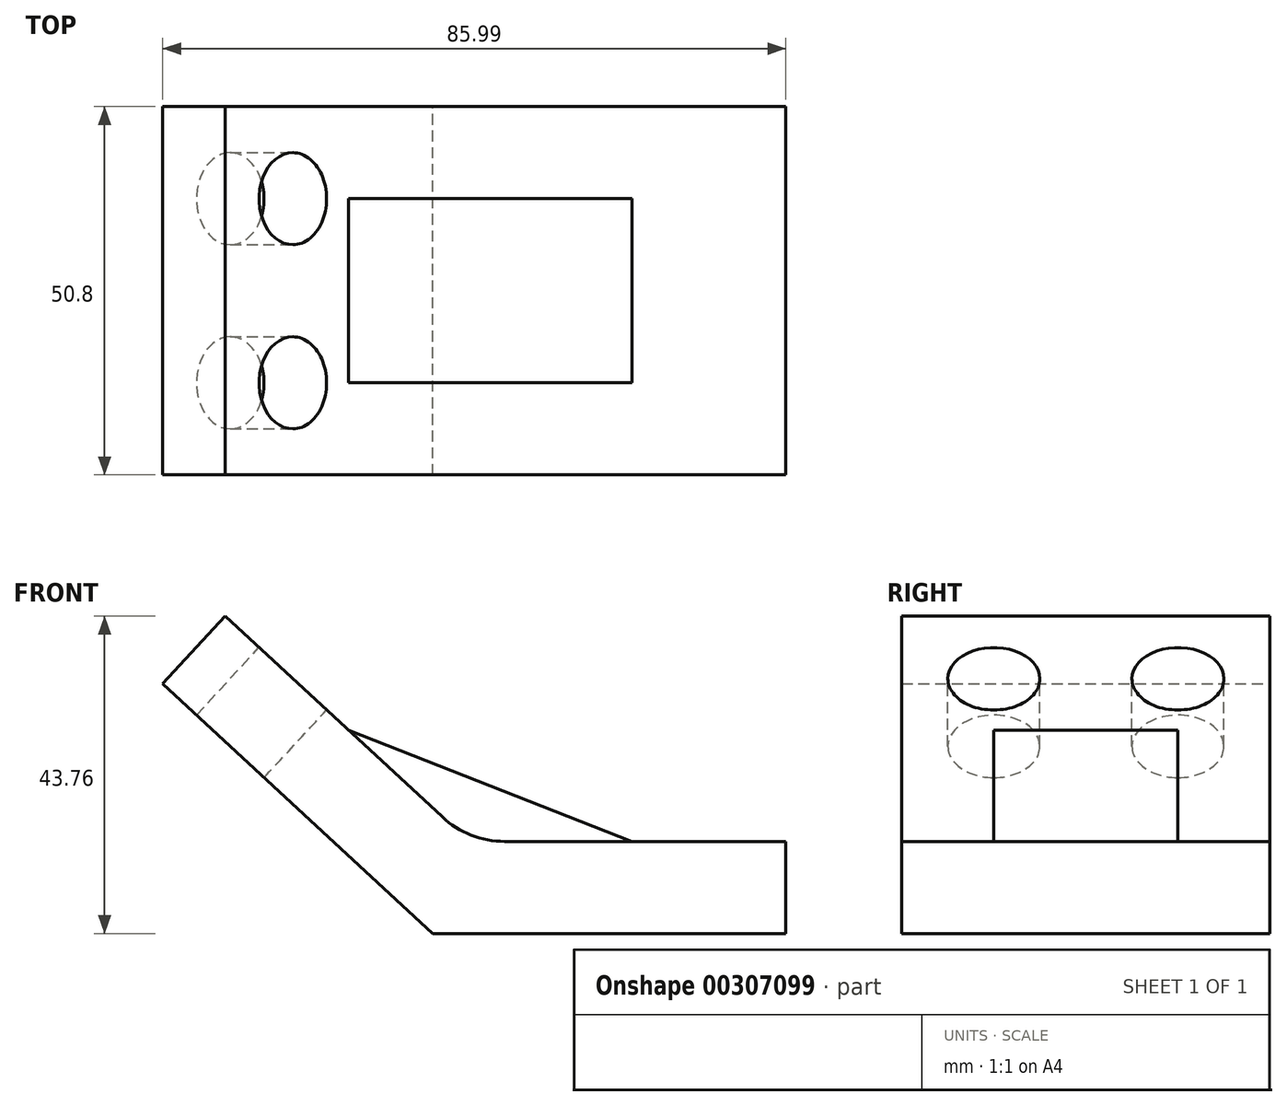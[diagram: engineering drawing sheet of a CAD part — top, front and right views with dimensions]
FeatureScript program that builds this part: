
annotation { "Feature Type Name" : "Feature", "Feature Type Description" : "" }
export const myFeature = defineFeature(function(context is Context, id is Id, definition is map)
    precondition{}
    {
        {
            var Q0;
            Q0=qCreatedBy(makeId("Front.planeOp"),FACE);
            var sketch = newSketch(context, id + "F0", { "sketchPlane" : qUnion([Q0])});
            skLineSegment(sketch, "E0", {"start": v(0, 0) * mm, "end": v(48.74, 0) * mm});
            skLineSegment(sketch, "E1", {"start": v(48.74, 0) * mm, "end": v(48.74, 12.7) * mm});
            skLineSegment(sketch, "E2", {"start": v(48.74, 12.7) * mm, "end": v(4.97, 12.7) * mm});
            skLineSegment(sketch, "E3", {"start": v(4.97, 12.7) * mm, "end": v(-28.63, 43.76) * mm});
            skLineSegment(sketch, "E4", {"start": v(-28.63, 43.76) * mm, "end": v(-37.25, 34.43) * mm});
            skLineSegment(sketch, "E5", {"start": v(-37.25, 34.43) * mm, "end": v(0, 0) * mm});
            skSolve(sketch);
        }
        {
            var Q0;
            Q0 = qSketchRegion(id + "F0", true);
            extrude(context, id + "F1", {"entities" : qUnion([Q0]), "endBound" : BoundingType.SYMMETRIC, "depth" : 50.8 * mm});
        }
        {
            var Q0;
            Q0=makeQuery(id+"F1.opExtrude","SWEPT_EDGE",EDGE,{"disambiguationData":[OSD([sQuery(id+"F0.wireOp",EDGE,"E2"),sQuery(id+"F0.wireOp",EDGE,"E3")])]});
            fillet(context, id + "F2", {"entities" : qUnion([Q0]), "radius" : 12.7 * mm, "tangentPropagation" : true, "allowEdgeOverflow" : false});
        }
        {
            var Q0;
            Q0=qCreatedBy(makeId("Front.planeOp"),FACE);
            var sketch = newSketch(context, id + "F3", { "sketchPlane" : qUnion([Q0])});
            skLineSegment(sketch, "E6", {"start": v(27.53, 12.7) * mm, "end": v(4.97, 12.7) * mm});
            skLineSegment(sketch, "E7", {"start": v(4.97, 12.7) * mm, "end": v(-11.6, 28.01) * mm});
            skLineSegment(sketch, "E8", {"start": v(-11.6, 28.01) * mm, "end": v(27.53, 12.7) * mm});
            skSolve(sketch);
        }
        {
            var Q0;
            Q0 = qSketchRegion(id + "F3", true);
            extrude(context, id + "F4", {"entities" : qUnion([Q0]), "operationType" : NewBodyOperationType.ADD, "endBound" : BoundingType.SYMMETRIC, "depth" : 25.4 * mm});
        }
        {
            var Q0;
            Q0=makeQuery(id+"F1.opExtrude","SWEPT_FACE",FACE,{"disambiguationData":[OSD([sQuery(id+"F0.wireOp",EDGE,"E3")])]});
            var sketch = newSketch(context, id + "F5", { "sketchPlane" : qUnion([Q0])});
            skCircle(sketch, "E9", {"center": v(-38.03, -12.7) * mm, "radius": 6.35 * mm});
            skCircle(sketch, "E10", {"center": v(-38.03, 12.7) * mm, "radius": 6.35 * mm});
            skSolve(sketch);
        }
        {
            var Q0;
            Q0 = qSketchRegion(id + "F5", true);
            extrude(context, id + "F6", {"entities" : qUnion([Q0]), "operationType" : NewBodyOperationType.REMOVE, "oppositeDirection" : true, "depth" : 25.4 * mm});
        }
    });
